# Revit family: Electronics_Commercial-Audio_Biamp_Power-Amplifier_PA240P
name_source: partatom
category: Communication Devices
units: mm (PartAtom-declared; Revit-internal decimal feet)

## family parameters
Cut with Voids When Loaded = No
Host = Face
Maintain Annotation Orientation = No
OmniClass Number = 23.85.10.11.14.14.17
OmniClass Title = Sound Amplifiers
Part Type = Normal
Room Calculation Point = No
Round Connector Dimension = Use Diameter
Shared = No

## types (1)
- PA240P
    Apparent Load = 525 VA
    Connector Description = Power supply
    Default Elevation = 48 "
    Depth = 14 "
    Description = PA240P 1-Channel Power Amplifier
    Height = 3 "
    Housing Material = Biamp - Metal - Black
    Manufacturer = Biamp
    Max Power Consumption = 525 W
    Model = PA240P
    Number of Poles = 1
    Power Factor = 1
    Product Documentation Link = https://downloads.biamp.com
    Product Page URL = https://www.biamp.com
    Product data url = https://bimobject.com
    Temperature Range = 90°C/ch + transformer 105°C
    URL = https://www.biamp.com
    Version = 1
    Voltage = 240 V
    Weight = 13.15 kgf
    Width = 17 "

## geometry (parser evidence)
native form markers: Sweep x5
no freeform markers — native parametric forms only
